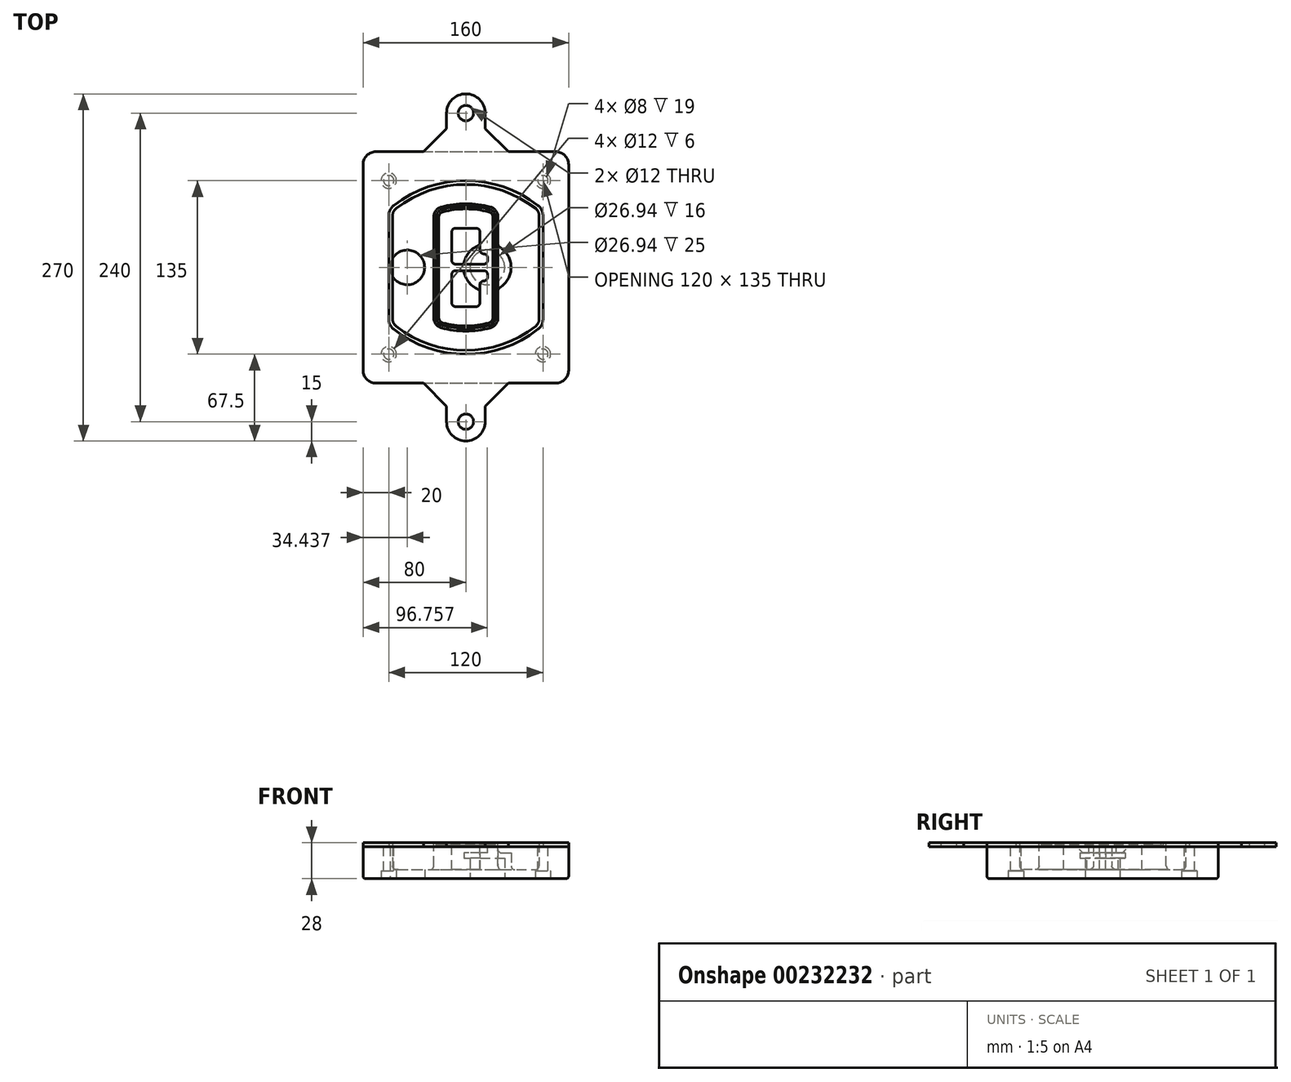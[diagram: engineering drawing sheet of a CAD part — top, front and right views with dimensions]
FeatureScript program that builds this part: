
annotation { "Feature Type Name" : "Feature", "Feature Type Description" : "" }
export const myFeature = defineFeature(function(context is Context, id is Id, definition is map)
    precondition{}
    {
        {
            var Q0;
            Q0=qCreatedBy(makeId("Top.planeOp"),FACE);
            var sketch = newSketch(context, id + "F0", { "sketchPlane" : qUnion([Q0])});
            skPoint(sketch, "E0.rect.middle", {"position": v(0, 0) * mm});
            skLineSegment(sketch, "E1.bottom", {"start": v(-70, -90) * mm, "end": v(70, -90) * mm});
            skLineSegment(sketch, "E1.top", {"start": v(-70, 90) * mm, "end": v(70, 90) * mm});
            skLineSegment(sketch, "E1.left", {"start": v(-80, -80) * mm, "end": v(-80, 80) * mm});
            skLineSegment(sketch, "E1.right", {"start": v(80, -80) * mm, "end": v(80, 80) * mm});
            skLineSegment(sketch, "E2", {"start": v(-80, 90) * mm, "end": v(80, -90) * mm, "construction": true});
            skLineSegment(sketch, "E3", {"start": v(80, 90) * mm, "end": v(-80, -90) * mm, "construction": true});
            skCircle(sketch, "E4", {"center": v(-60, 67.5) * mm, "radius": 4 * mm});
            skCircle(sketch, "E5", {"center": v(60, 67.5) * mm, "radius": 4 * mm});
            skCircle(sketch, "E6", {"center": v(60, -67.5) * mm, "radius": 4 * mm});
            skCircle(sketch, "E7", {"center": v(-60, -67.5) * mm, "radius": 4 * mm});
            skLineSegment(sketch, "E8", {"start": v(-60, 67.5) * mm, "end": v(60, 67.5) * mm, "construction": true});
            skLineSegment(sketch, "E9", {"start": v(60, 67.5) * mm, "end": v(60, -67.5) * mm, "construction": true});
            skLineSegment(sketch, "E10", {"start": v(60, -67.5) * mm, "end": v(-60, -67.5) * mm, "construction": true});
            skLineSegment(sketch, "E11", {"start": v(-60, -67.5) * mm, "end": v(-60, 67.5) * mm, "construction": true});
            skLineSegment(sketch, "E12", {"start": v(-60, 40.3) * mm, "end": v(-60, -40.3) * mm});
            skLineSegment(sketch, "E13", {"start": v(60, 40.3) * mm, "end": v(60, -40.3) * mm});
            skArc(sketch, "E14", {"start": v(56.15, 48.18) * mm, "mid": v(0, 67.5) * mm, "end": v(-56.15, 48.18) * mm});
            skArc(sketch, "E15", {"start": v(-56.15, -48.18) * mm, "mid": v(0, -67.5) * mm, "end": v(56.15, -48.18) * mm});
            skLineSegment(sketch, "E16", {"start": v(-60, 0) * mm, "end": v(60, 0) * mm, "construction": true});
            skPoint(sketch, "E17.visualSharp", {"position": v(-60, -45) * mm});
            skArc(sketch, "E17.filletArc", {"start": v(-60, -40.3) * mm, "mid": v(-58.99, -44.68) * mm, "end": v(-56.15, -48.18) * mm});
            skPoint(sketch, "E18.visualSharp", {"position": v(-60, 45) * mm});
            skArc(sketch, "E18.filletArc", {"start": v(-56.15, 48.18) * mm, "mid": v(-58.99, 44.68) * mm, "end": v(-60, 40.3) * mm});
            skPoint(sketch, "E19.visualSharp", {"position": v(60, 45) * mm});
            skArc(sketch, "E19.filletArc", {"start": v(60, 40.3) * mm, "mid": v(58.99, 44.68) * mm, "end": v(56.15, 48.18) * mm});
            skPoint(sketch, "E20.visualSharp", {"position": v(60, -45) * mm});
            skArc(sketch, "E20.filletArc", {"start": v(56.15, -48.18) * mm, "mid": v(58.99, -44.68) * mm, "end": v(60, -40.3) * mm});
            skPoint(sketch, "E21.visualSharp", {"position": v(-80, 90) * mm});
            skArc(sketch, "E21.filletArc", {"start": v(-70, 90) * mm, "mid": v(-77.07, 87.07) * mm, "end": v(-80, 80) * mm});
            skPoint(sketch, "E22.visualSharp", {"position": v(80, 90) * mm});
            skArc(sketch, "E22.filletArc", {"start": v(80, 80) * mm, "mid": v(77.07, 87.07) * mm, "end": v(70, 90) * mm});
            skPoint(sketch, "E23.visualSharp", {"position": v(80, -90) * mm});
            skArc(sketch, "E23.filletArc", {"start": v(70, -90) * mm, "mid": v(77.07, -87.07) * mm, "end": v(80, -80) * mm});
            skPoint(sketch, "E24.visualSharp", {"position": v(-80, -90) * mm});
            skArc(sketch, "E24.filletArc", {"start": v(-80, -80) * mm, "mid": v(-77.07, -87.07) * mm, "end": v(-70, -90) * mm});
            skArc(sketch, "E25.0", {"start": v(57, 40.3) * mm, "mid": v(56.3, 43.36) * mm, "end": v(54.3, 45.81) * mm});
            skLineSegment(sketch, "E25.1", {"start": v(57, 40.3) * mm, "end": v(57, -40.3) * mm});
            skArc(sketch, "E25.2", {"start": v(54.3, -45.81) * mm, "mid": v(56.3, -43.36) * mm, "end": v(57, -40.3) * mm});
            skArc(sketch, "E25.3", {"start": v(-54.3, -45.81) * mm, "mid": v(0, -64.5) * mm, "end": v(54.3, -45.81) * mm});
            skArc(sketch, "E25.4", {"start": v(-57, -40.3) * mm, "mid": v(-56.3, -43.36) * mm, "end": v(-54.3, -45.81) * mm});
            skArc(sketch, "E25.5", {"start": v(54.3, 45.81) * mm, "mid": v(0, 64.5) * mm, "end": v(-54.3, 45.81) * mm});
            skLineSegment(sketch, "E25.6", {"start": v(-57, 40.3) * mm, "end": v(-57, -40.3) * mm});
            skArc(sketch, "E25.7", {"start": v(-54.3, 45.81) * mm, "mid": v(-56.3, 43.36) * mm, "end": v(-57, 40.3) * mm});
            skArc(sketch, "E26.0", {"start": v(-58.62, 51.33) * mm, "mid": v(-62.58, 46.43) * mm, "end": v(-64, 40.3) * mm});
            skArc(sketch, "E26.1", {"start": v(58.62, 51.33) * mm, "mid": v(0, 71.5) * mm, "end": v(-58.62, 51.33) * mm});
            skArc(sketch, "E26.2", {"start": v(64, 40.3) * mm, "mid": v(62.58, 46.43) * mm, "end": v(58.62, 51.33) * mm});
            skLineSegment(sketch, "E26.3", {"start": v(64, 40.3) * mm, "end": v(64, -40.3) * mm});
            skArc(sketch, "E26.4", {"start": v(58.62, -51.33) * mm, "mid": v(62.58, -46.43) * mm, "end": v(64, -40.3) * mm});
            skLineSegment(sketch, "E26.5", {"start": v(-64, 40.3) * mm, "end": v(-64, -40.3) * mm});
            skArc(sketch, "E26.6", {"start": v(-58.62, -51.33) * mm, "mid": v(0, -71.5) * mm, "end": v(58.62, -51.33) * mm});
            skArc(sketch, "E26.7", {"start": v(-64, -40.3) * mm, "mid": v(-62.58, -46.43) * mm, "end": v(-58.62, -51.33) * mm});
            skSolve(sketch);
        }
        {
            var Q0;
            Q0=makeQuery(id+"F0.imprint","IMPRINT",FACE,{"disambiguationData":[TD([[makeQuery(id+"F0.imprint","IMPRINT",EDGE,{"derivedFrom":sQuery(id+"F0.wireOp",EDGE,"E1.bottom")}),1.0]])]});
            var Q1;
            Q1=makeQuery(id+"F0.imprint","IMPRINT",FACE,{"disambiguationData":[TD([[makeQuery(id+"F0.imprint","IMPRINT",EDGE,{"derivedFrom":sQuery(id+"F0.wireOp",EDGE,"E12")}),1.0]])]});
            var Q2;
            Q2=makeQuery(id+"F0.imprint","IMPRINT",FACE,{"disambiguationData":[TD([[makeQuery(id+"F0.imprint","IMPRINT",EDGE,{"derivedFrom":sQuery(id+"F0.wireOp",EDGE,"E25.0")}),1.0]])]});
            var Q3;
            Q3=makeQuery(id+"F0.imprint","IMPRINT",FACE,{"disambiguationData":[TD([[makeQuery(id+"F0.imprint","IMPRINT",EDGE,{"derivedFrom":sQuery(id+"F0.wireOp",EDGE,"E12")}),-1.0]])]});
            extrude(context, id + "F1", {"entities" : qUnion([Q0, Q1, Q2, Q3]), "oppositeDirection" : true, "depth" : 25 * mm});
        }
        {
            var Q0;
            Q0=makeQuery(id+"F0.imprint","IMPRINT",FACE,{"disambiguationData":[TD([[makeQuery(id+"F0.imprint","IMPRINT",EDGE,{"derivedFrom":sQuery(id+"F0.wireOp",EDGE,"E12")}),1.0]])]});
            extrude(context, id + "F2", {"entities" : qUnion([Q0]), "operationType" : NewBodyOperationType.ADD, "depth" : 3 * mm});
        }
        {
            var Q0;
            Q0=makeQuery(id+"F0.imprint","IMPRINT",FACE,{"disambiguationData":[TD([[makeQuery(id+"F0.imprint","IMPRINT",EDGE,{"derivedFrom":sQuery(id+"F0.wireOp",EDGE,"E25.0")}),1.0]])]});
            extrude(context, id + "F3", {"entities" : qUnion([Q0]), "operationType" : NewBodyOperationType.REMOVE, "oppositeDirection" : true, "depth" : 18 * mm});
        }
        {
            var Q0;
            Q0=makeQuery(id+"F2.opExtrude","CAP_FACE",FACE,{"disambiguationData":[OSD([sQuery(id+"F0.wireOp",EDGE,"E12"),sQuery(id+"F0.wireOp",EDGE,"E13"),sQuery(id+"F0.wireOp",EDGE,"E14"),sQuery(id+"F0.wireOp",EDGE,"E15"),sQuery(id+"F0.wireOp",EDGE,"E17.filletArc"),sQuery(id+"F0.wireOp",EDGE,"E18.filletArc"),sQuery(id+"F0.wireOp",EDGE,"E19.filletArc"),sQuery(id+"F0.wireOp",EDGE,"E20.filletArc"),sQuery(id+"F0.wireOp",EDGE,"E25.0"),sQuery(id+"F0.wireOp",EDGE,"E25.1"),sQuery(id+"F0.wireOp",EDGE,"E25.2"),sQuery(id+"F0.wireOp",EDGE,"E25.3"),sQuery(id+"F0.wireOp",EDGE,"E25.4"),sQuery(id+"F0.wireOp",EDGE,"E25.5"),sQuery(id+"F0.wireOp",EDGE,"E25.6"),sQuery(id+"F0.wireOp",EDGE,"E25.7")])],"isStart":false});
            var sketch = newSketch(context, id + "F4", { "sketchPlane" : qUnion([Q0])});
            skArc(sketch, "E27.0", {"start": v(-19.08, -46.97) * mm, "mid": v(0, -49.5) * mm, "end": v(19.08, -46.97) * mm});
            skArc(sketch, "E28.0", {"start": v(19.08, 46.97) * mm, "mid": v(0, 49.5) * mm, "end": v(-19.08, 46.97) * mm});
            skLineSegment(sketch, "E29", {"start": v(-25, 39.25) * mm, "end": v(-25, -39.25) * mm});
            skLineSegment(sketch, "E30", {"start": v(25, 39.25) * mm, "end": v(25, -39.25) * mm});
            skLineSegment(sketch, "E31", {"start": v(-25, 45.1) * mm, "end": v(25, 45.1) * mm, "construction": true});
            skLineSegment(sketch, "E32", {"start": v(-25, -45.1) * mm, "end": v(25, -45.1) * mm, "construction": true});
            skPoint(sketch, "E33.visualSharp", {"position": v(-25, 45.1) * mm});
            skArc(sketch, "E33.filletArc", {"start": v(-19.08, 46.97) * mm, "mid": v(-23.35, 44.11) * mm, "end": v(-25, 39.25) * mm});
            skPoint(sketch, "E34.visualSharp", {"position": v(25, 45.1) * mm});
            skArc(sketch, "E34.filletArc", {"start": v(25, 39.25) * mm, "mid": v(23.35, 44.11) * mm, "end": v(19.08, 46.97) * mm});
            skPoint(sketch, "E35.visualSharp", {"position": v(25, -45.1) * mm});
            skArc(sketch, "E35.filletArc", {"start": v(19.08, -46.97) * mm, "mid": v(23.35, -44.11) * mm, "end": v(25, -39.25) * mm});
            skPoint(sketch, "E36.visualSharp", {"position": v(-25, -45.1) * mm});
            skArc(sketch, "E36.filletArc", {"start": v(-25, -39.25) * mm, "mid": v(-23.35, -44.11) * mm, "end": v(-19.08, -46.97) * mm});
            skArc(sketch, "E37.0", {"start": v(54.3, 45.81) * mm, "mid": v(0, 64.5) * mm, "end": v(-54.3, 45.81) * mm});
            skArc(sketch, "E37.1", {"start": v(-54.3, 45.81) * mm, "mid": v(-56.3, 43.36) * mm, "end": v(-57, 40.3) * mm});
            skLineSegment(sketch, "E37.2", {"start": v(-57, 40.3) * mm, "end": v(-57, -40.3) * mm});
            skArc(sketch, "E37.3", {"start": v(-57, -40.3) * mm, "mid": v(-56.3, -43.36) * mm, "end": v(-54.3, -45.81) * mm});
            skArc(sketch, "E37.4", {"start": v(-54.3, -45.81) * mm, "mid": v(0, -64.5) * mm, "end": v(54.3, -45.81) * mm});
            skArc(sketch, "E37.5", {"start": v(54.3, -45.81) * mm, "mid": v(56.3, -43.36) * mm, "end": v(57, -40.3) * mm});
            skLineSegment(sketch, "E37.6", {"start": v(57, 40.3) * mm, "end": v(57, -40.3) * mm});
            skArc(sketch, "E37.7", {"start": v(57, 40.3) * mm, "mid": v(56.3, 43.36) * mm, "end": v(54.3, 45.81) * mm});
            skLineSegment(sketch, "E38.0", {"start": v(23, 39.25) * mm, "end": v(23, -39.25) * mm});
            skArc(sketch, "E38.1", {"start": v(18.56, -45.04) * mm, "mid": v(21.76, -42.9) * mm, "end": v(23, -39.25) * mm});
            skArc(sketch, "E38.2", {"start": v(-18.56, -45.04) * mm, "mid": v(0, -47.5) * mm, "end": v(18.56, -45.04) * mm});
            skArc(sketch, "E38.3", {"start": v(-23, -39.25) * mm, "mid": v(-21.76, -42.9) * mm, "end": v(-18.56, -45.04) * mm});
            skLineSegment(sketch, "E38.4", {"start": v(-23, 39.25) * mm, "end": v(-23, -39.25) * mm});
            skArc(sketch, "E38.5", {"start": v(23, 39.25) * mm, "mid": v(21.76, 42.9) * mm, "end": v(18.56, 45.04) * mm});
            skArc(sketch, "E38.6", {"start": v(-18.56, 45.04) * mm, "mid": v(-21.76, 42.9) * mm, "end": v(-23, 39.25) * mm});
            skArc(sketch, "E38.7", {"start": v(18.56, 45.04) * mm, "mid": v(0, 47.5) * mm, "end": v(-18.56, 45.04) * mm});
            skArc(sketch, "E39.0", {"start": v(21, 39.25) * mm, "mid": v(20.18, 41.68) * mm, "end": v(18.04, 43.1) * mm});
            skLineSegment(sketch, "E39.1", {"start": v(21, 39.25) * mm, "end": v(21, -39.25) * mm});
            skArc(sketch, "E39.2", {"start": v(18.04, -43.1) * mm, "mid": v(20.18, -41.68) * mm, "end": v(21, -39.25) * mm});
            skArc(sketch, "E39.3", {"start": v(-18.04, -43.1) * mm, "mid": v(0, -45.5) * mm, "end": v(18.04, -43.1) * mm});
            skArc(sketch, "E39.4", {"start": v(-21, -39.25) * mm, "mid": v(-20.18, -41.68) * mm, "end": v(-18.04, -43.1) * mm});
            skArc(sketch, "E39.5", {"start": v(18.04, 43.1) * mm, "mid": v(0, 45.5) * mm, "end": v(-18.04, 43.1) * mm});
            skLineSegment(sketch, "E39.6", {"start": v(-21, 39.25) * mm, "end": v(-21, -39.25) * mm});
            skArc(sketch, "E39.7", {"start": v(-18.04, 43.1) * mm, "mid": v(-20.18, 41.68) * mm, "end": v(-21, 39.25) * mm});
            skLineSegment(sketch, "E40", {"start": v(-25, 0) * mm, "end": v(25, 0) * mm, "construction": true});
            skLineSegment(sketch, "E41", {"start": v(-11, 5.5) * mm, "end": v(-11, 27.5) * mm});
            skLineSegment(sketch, "E42", {"start": v(-8, 30.5) * mm, "end": v(8, 30.5) * mm});
            skLineSegment(sketch, "E43", {"start": v(11, 27.5) * mm, "end": v(11, 13.5) * mm});
            skLineSegment(sketch, "E44", {"start": v(14, 10.5) * mm, "end": v(14, 10.5) * mm});
            skLineSegment(sketch, "E45", {"start": v(17, 7.5) * mm, "end": v(17, 5.5) * mm});
            skLineSegment(sketch, "E46", {"start": v(14, 2.5) * mm, "end": v(-8, 2.5) * mm});
            skPoint(sketch, "E47.visualSharp", {"position": v(-11, 30.5) * mm});
            skArc(sketch, "E47.filletArc", {"start": v(-8, 30.5) * mm, "mid": v(-10.12, 29.62) * mm, "end": v(-11, 27.5) * mm});
            skPoint(sketch, "E48.visualSharp", {"position": v(11, 30.5) * mm});
            skArc(sketch, "E48.filletArc", {"start": v(11, 27.5) * mm, "mid": v(10.12, 29.62) * mm, "end": v(8, 30.5) * mm});
            skPoint(sketch, "E49.visualSharp", {"position": v(11, 10.5) * mm});
            skArc(sketch, "E49.filletArc", {"start": v(11, 13.5) * mm, "mid": v(11.88, 11.38) * mm, "end": v(14, 10.5) * mm});
            skPoint(sketch, "E50.visualSharp", {"position": v(17, 10.5) * mm});
            skArc(sketch, "E50.filletArc", {"start": v(17, 7.5) * mm, "mid": v(16.12, 9.62) * mm, "end": v(14, 10.5) * mm});
            skPoint(sketch, "E51.visualSharp", {"position": v(17, 2.5) * mm});
            skArc(sketch, "E51.filletArc", {"start": v(14, 2.5) * mm, "mid": v(16.12, 3.38) * mm, "end": v(17, 5.5) * mm});
            skPoint(sketch, "E52.visualSharp", {"position": v(-11, 2.5) * mm});
            skArc(sketch, "E52.filletArc", {"start": v(-11, 5.5) * mm, "mid": v(-10.12, 3.38) * mm, "end": v(-8, 2.5) * mm});
            skLineSegment(sketch, "E53.0.MirrorCS", {"start": v(14, -2.5) * mm, "end": v(-8, -2.5) * mm});
            skArc(sketch, "E54.0.MirrorCS", {"start": v(-11, -5.5) * mm, "mid": v(-10.12, -3.38) * mm, "end": v(-8, -2.5) * mm});
            skLineSegment(sketch, "E55.0.MirrorCS", {"start": v(-11, -5.5) * mm, "end": v(-11, -27.5) * mm});
            skArc(sketch, "E56.0.MirrorCS", {"start": v(-8, -30.5) * mm, "mid": v(-10.12, -29.62) * mm, "end": v(-11, -27.5) * mm});
            skLineSegment(sketch, "E57.0.MirrorCS", {"start": v(-8, -30.5) * mm, "end": v(8, -30.5) * mm});
            skArc(sketch, "E58.0.MirrorCS", {"start": v(11, -27.5) * mm, "mid": v(10.12, -29.62) * mm, "end": v(8, -30.5) * mm});
            skLineSegment(sketch, "E59.0.MirrorCS", {"start": v(11, -27.5) * mm, "end": v(11, -13.5) * mm});
            skArc(sketch, "E60.0.MirrorCS", {"start": v(11, -13.5) * mm, "mid": v(11.88, -11.38) * mm, "end": v(14, -10.5) * mm});
            skArc(sketch, "E61.0.MirrorCS", {"start": v(17, -7.5) * mm, "mid": v(16.12, -9.62) * mm, "end": v(14, -10.5) * mm});
            skLineSegment(sketch, "E62.0.MirrorCS", {"start": v(17, -7.5) * mm, "end": v(17, -5.5) * mm});
            skArc(sketch, "E63.0.MirrorCS", {"start": v(14, -2.5) * mm, "mid": v(16.12, -3.38) * mm, "end": v(17, -5.5) * mm});
            skSolve(sketch);
        }
        {
            var Q0;
            Q0=makeQuery(id+"F4.imprint","IMPRINT",FACE,{"disambiguationData":[TD([[makeQuery(id+"F4.imprint","IMPRINT",EDGE,{"derivedFrom":sQuery(id+"F4.wireOp",EDGE,"E27.0")}),1.0]])]});
            var Q1;
            Q1=makeQuery(id+"F4.imprint","IMPRINT",FACE,{"disambiguationData":[TD([[makeQuery(id+"F4.imprint","IMPRINT",EDGE,{"derivedFrom":sQuery(id+"F4.wireOp",EDGE,"E38.0")}),-1.0]])]});
            var Q2;
            Q2=makeQuery(id+"F4.imprint","IMPRINT",FACE,{"disambiguationData":[TD([[makeQuery(id+"F4.imprint","IMPRINT",EDGE,{"derivedFrom":sQuery(id+"F4.wireOp",EDGE,"E39.0")}),1.0]])]});
            extrude(context, id + "F5", {"entities" : qUnion([Q0, Q1, Q2]), "operationType" : NewBodyOperationType.ADD, "endBound" : BoundingType.UP_TO_NEXT, "oppositeDirection" : true, "depth" : 25 * mm});
        }
        {
            var Q0;
            Q0=makeQuery(id+"F4.imprint","IMPRINT",FACE,{"disambiguationData":[TD([[makeQuery(id+"F4.imprint","IMPRINT",EDGE,{"derivedFrom":sQuery(id+"F4.wireOp",EDGE,"E38.0")}),-1.0]])]});
            extrude(context, id + "F6", {"entities" : qUnion([Q0]), "operationType" : NewBodyOperationType.REMOVE, "oppositeDirection" : true, "depth" : 2 * mm});
        }
        {
            var Q0;
            Q0=makeQuery(id+"F1.opExtrude","CAP_FACE",FACE,{"disambiguationData":[OSD([sQuery(id+"F0.wireOp",EDGE,"E1.bottom"),sQuery(id+"F0.wireOp",EDGE,"E1.top"),sQuery(id+"F0.wireOp",EDGE,"E1.left"),sQuery(id+"F0.wireOp",EDGE,"E1.right"),sQuery(id+"F0.wireOp",EDGE,"E4"),sQuery(id+"F0.wireOp",EDGE,"E5"),sQuery(id+"F0.wireOp",EDGE,"E6"),sQuery(id+"F0.wireOp",EDGE,"E7"),sQuery(id+"F0.wireOp",EDGE,"E21.filletArc"),sQuery(id+"F0.wireOp",EDGE,"E22.filletArc"),sQuery(id+"F0.wireOp",EDGE,"E23.filletArc"),sQuery(id+"F0.wireOp",EDGE,"E24.filletArc")])],"isStart":false});
            var sketch = newSketch(context, id + "F7", { "sketchPlane" : qUnion([Q0])});
            skCircle(sketch, "E64", {"center": v(16.76, 0) * mm, "radius": 13.47 * mm});
            skCircle(sketch, "E65", {"center": v(-45.56, 0) * mm, "radius": 13.47 * mm});
            skLineSegment(sketch, "E66", {"start": v(80, 0) * mm, "end": v(-80, 0) * mm});
            skCircle(sketch, "E67", {"center": v(16.76, 0) * mm, "radius": 18.47 * mm});
            skCircle(sketch, "E68", {"center": v(60, -67.5) * mm, "radius": 6 * mm});
            skCircle(sketch, "E69", {"center": v(-60, -67.5) * mm, "radius": 6 * mm});
            skCircle(sketch, "E70", {"center": v(-60, 67.5) * mm, "radius": 6 * mm});
            skCircle(sketch, "E71", {"center": v(60, 67.5) * mm, "radius": 6 * mm});
            skSolve(sketch);
        }
        {
            var Q0;
            {var subQ1=sQuery(id+"F7.wireOp",EDGE,"E66");var subQ4=sQuery(id+"F7.wireOp",EDGE,"E64");var subQ6=makeQuery(id+"F7.imprint","INTERSECT",VERTEX,{"disambiguationData":[OD(0.0)],"derivedFrom":[subQ4,subQ1]});Q0=makeQuery(id+"F7.imprint","IMPRINT",FACE,{"disambiguationData":[TD([[makeQuery(id+"F7.imprint","IMPRINT",EDGE,{"disambiguationData":[TD([[subQ6,-1.0]])],"derivedFrom":subQ4}),-1.0]])]});}
            var Q1;
            {var subQ0=sQuery(id+"F7.wireOp",EDGE,"E66");var subQ1=sQuery(id+"F7.wireOp",EDGE,"E64");var subQ3=makeQuery(id+"F7.imprint","INTERSECT",VERTEX,{"disambiguationData":[OD(0.0)],"derivedFrom":[subQ1,subQ0]});Q1=makeQuery(id+"F7.imprint","IMPRINT",FACE,{"disambiguationData":[TD([[makeQuery(id+"F7.imprint","IMPRINT",EDGE,{"disambiguationData":[TD([[subQ3,-1.0]])],"derivedFrom":subQ1}),1.0]])]});}
            var Q2;
            {var subQ0=sQuery(id+"F7.wireOp",EDGE,"E66");var subQ1=sQuery(id+"F7.wireOp",EDGE,"E64");var subQ3=makeQuery(id+"F7.imprint","INTERSECT",VERTEX,{"disambiguationData":[OD(0.0)],"derivedFrom":[subQ1,subQ0]});Q2=makeQuery(id+"F7.imprint","IMPRINT",FACE,{"disambiguationData":[TD([[makeQuery(id+"F7.imprint","IMPRINT",EDGE,{"disambiguationData":[TD([[subQ3,1.0]])],"derivedFrom":subQ1}),1.0]])]});}
            var Q3;
            {var subQ1=sQuery(id+"F7.wireOp",EDGE,"E66");var subQ4=sQuery(id+"F7.wireOp",EDGE,"E64");var subQ6=makeQuery(id+"F7.imprint","INTERSECT",VERTEX,{"disambiguationData":[OD(0.0)],"derivedFrom":[subQ4,subQ1]});Q3=makeQuery(id+"F7.imprint","IMPRINT",FACE,{"disambiguationData":[TD([[makeQuery(id+"F7.imprint","IMPRINT",EDGE,{"disambiguationData":[TD([[subQ6,1.0]])],"derivedFrom":subQ4}),-1.0]])]});}
            extrude(context, id + "F8", {"entities" : qUnion([Q0, Q1, Q2, Q3]), "operationType" : NewBodyOperationType.ADD, "oppositeDirection" : true, "depth" : 20 * mm});
        }
        {
            var Q0;
            {var subQ0=sQuery(id+"F7.wireOp",EDGE,"E66");var subQ1=sQuery(id+"F7.wireOp",EDGE,"E64");var subQ3=makeQuery(id+"F7.imprint","INTERSECT",VERTEX,{"disambiguationData":[OD(0.0)],"derivedFrom":[subQ1,subQ0]});Q0=makeQuery(id+"F7.imprint","IMPRINT",FACE,{"disambiguationData":[TD([[makeQuery(id+"F7.imprint","IMPRINT",EDGE,{"disambiguationData":[TD([[subQ3,-1.0]])],"derivedFrom":subQ1}),1.0]])]});}
            var Q1;
            {var subQ0=sQuery(id+"F7.wireOp",EDGE,"E66");var subQ1=sQuery(id+"F7.wireOp",EDGE,"E64");var subQ3=makeQuery(id+"F7.imprint","INTERSECT",VERTEX,{"disambiguationData":[OD(0.0)],"derivedFrom":[subQ1,subQ0]});Q1=makeQuery(id+"F7.imprint","IMPRINT",FACE,{"disambiguationData":[TD([[makeQuery(id+"F7.imprint","IMPRINT",EDGE,{"disambiguationData":[TD([[subQ3,1.0]])],"derivedFrom":subQ1}),1.0]])]});}
            extrude(context, id + "F9", {"entities" : qUnion([Q0, Q1]), "operationType" : NewBodyOperationType.REMOVE, "oppositeDirection" : true, "depth" : 16 * mm});
        }
        {
            var Q0;
            {var subQ0=sQuery(id+"F7.wireOp",EDGE,"E66");var subQ1=sQuery(id+"F7.wireOp",EDGE,"E65");var subQ3=makeQuery(id+"F7.imprint","INTERSECT",VERTEX,{"disambiguationData":[OD(0.0)],"derivedFrom":[subQ1,subQ0]});Q0=makeQuery(id+"F7.imprint","IMPRINT",FACE,{"disambiguationData":[TD([[makeQuery(id+"F7.imprint","IMPRINT",EDGE,{"disambiguationData":[TD([[subQ3,-1.0]])],"derivedFrom":subQ1}),1.0]])]});}
            var Q1;
            {var subQ0=sQuery(id+"F7.wireOp",EDGE,"E66");var subQ1=sQuery(id+"F7.wireOp",EDGE,"E65");var subQ3=makeQuery(id+"F7.imprint","INTERSECT",VERTEX,{"disambiguationData":[OD(0.0)],"derivedFrom":[subQ1,subQ0]});Q1=makeQuery(id+"F7.imprint","IMPRINT",FACE,{"disambiguationData":[TD([[makeQuery(id+"F7.imprint","IMPRINT",EDGE,{"disambiguationData":[TD([[subQ3,1.0]])],"derivedFrom":subQ1}),1.0]])]});}
            extrude(context, id + "F10", {"entities" : qUnion([Q0, Q1]), "operationType" : NewBodyOperationType.REMOVE, "oppositeDirection" : true, "depth" : 25 * mm});
        }
        {
            var Q0;
            Q0=makeQuery(id+"F7.imprint","IMPRINT",FACE,{"disambiguationData":[TD([[makeQuery(id+"F7.imprint","IMPRINT",EDGE,{"derivedFrom":sQuery(id+"F7.wireOp",EDGE,"E68")}),1.0]])]});
            var Q1;
            Q1=makeQuery(id+"F7.imprint","IMPRINT",FACE,{"disambiguationData":[TD([[makeQuery(id+"F7.imprint","IMPRINT",EDGE,{"derivedFrom":makeQuery(id+"F1.opExtrude","CAP_EDGE",EDGE,{"disambiguationData":[OSD([sQuery(id+"F0.wireOp",EDGE,"E5")])],"isStart":false})}),-1.0]])]});
            var Q2;
            Q2=makeQuery(id+"F7.imprint","IMPRINT",FACE,{"disambiguationData":[TD([[makeQuery(id+"F7.imprint","IMPRINT",EDGE,{"derivedFrom":sQuery(id+"F7.wireOp",EDGE,"E69")}),1.0]])]});
            var Q3;
            Q3=makeQuery(id+"F7.imprint","IMPRINT",FACE,{"disambiguationData":[TD([[makeQuery(id+"F7.imprint","IMPRINT",EDGE,{"derivedFrom":makeQuery(id+"F1.opExtrude","CAP_EDGE",EDGE,{"disambiguationData":[OSD([sQuery(id+"F0.wireOp",EDGE,"E4")])],"isStart":false})}),-1.0]])]});
            var Q4;
            Q4=makeQuery(id+"F7.imprint","IMPRINT",FACE,{"disambiguationData":[TD([[makeQuery(id+"F7.imprint","IMPRINT",EDGE,{"derivedFrom":sQuery(id+"F7.wireOp",EDGE,"E70")}),1.0]])]});
            var Q5;
            Q5=makeQuery(id+"F7.imprint","IMPRINT",FACE,{"disambiguationData":[TD([[makeQuery(id+"F7.imprint","IMPRINT",EDGE,{"derivedFrom":makeQuery(id+"F1.opExtrude","CAP_EDGE",EDGE,{"disambiguationData":[OSD([sQuery(id+"F0.wireOp",EDGE,"E7")])],"isStart":false})}),-1.0]])]});
            var Q6;
            Q6=makeQuery(id+"F7.imprint","IMPRINT",FACE,{"disambiguationData":[TD([[makeQuery(id+"F7.imprint","IMPRINT",EDGE,{"derivedFrom":sQuery(id+"F7.wireOp",EDGE,"E71")}),1.0]])]});
            var Q7;
            Q7=makeQuery(id+"F7.imprint","IMPRINT",FACE,{"disambiguationData":[TD([[makeQuery(id+"F7.imprint","IMPRINT",EDGE,{"derivedFrom":makeQuery(id+"F1.opExtrude","CAP_EDGE",EDGE,{"disambiguationData":[OSD([sQuery(id+"F0.wireOp",EDGE,"E6")])],"isStart":false})}),-1.0]])]});
            extrude(context, id + "F11", {"entities" : qUnion([Q0, Q1, Q2, Q3, Q4, Q5, Q6, Q7]), "operationType" : NewBodyOperationType.REMOVE, "oppositeDirection" : true, "depth" : 6 * mm});
        }
        {
            var Q0;
            Q0=makeQuery(id+"F9.boolean.opBoolean","COPY",FACE,{"derivedFrom":makeQuery(id+"F9.opExtrude","CAP_FACE",FACE,{"disambiguationData":[OSD([sQuery(id+"F7.wireOp",EDGE,"E64")])],"isStart":false})});
            var sketch = newSketch(context, id + "F12", { "sketchPlane" : qUnion([Q0])});
            skArc(sketch, "E72.0", {"start": v(11, 17.55) * mm, "mid": v(2.57, 11.82) * mm, "end": v(-1.54, 2.5) * mm});
            skArc(sketch, "E72.1", {"start": v(-1.54, -2.5) * mm, "mid": v(2.57, -11.82) * mm, "end": v(11, -17.55) * mm});
            skLineSegment(sketch, "E73", {"start": v(-1.54, -2.5) * mm, "end": v(14, -2.5) * mm});
            skLineSegment(sketch, "E74.0", {"start": v(14, 2.5) * mm, "end": v(-1.54, 2.5) * mm});
            skArc(sketch, "E74.1", {"start": v(14, 2.5) * mm, "mid": v(16.12, 3.38) * mm, "end": v(17, 5.5) * mm});
            skLineSegment(sketch, "E74.2", {"start": v(17, 7.5) * mm, "end": v(17, 5.5) * mm});
            skArc(sketch, "E74.3", {"start": v(17, 7.5) * mm, "mid": v(16.12, 9.62) * mm, "end": v(14, 10.5) * mm});
            skArc(sketch, "E74.4", {"start": v(11, 13.5) * mm, "mid": v(11.88, 11.38) * mm, "end": v(14, 10.5) * mm});
            skLineSegment(sketch, "E74.5", {"start": v(11, 17.55) * mm, "end": v(11, 13.5) * mm});
            skLineSegment(sketch, "E74.7", {"start": v(14, -2.5) * mm, "end": v(-1.54, -2.5) * mm});
            skArc(sketch, "E74.8", {"start": v(14, -2.5) * mm, "mid": v(16.12, -3.38) * mm, "end": v(17, -5.5) * mm});
            skLineSegment(sketch, "E74.9", {"start": v(17, -7.5) * mm, "end": v(17, -5.5) * mm});
            skArc(sketch, "E74.10", {"start": v(17, -7.5) * mm, "mid": v(16.12, -9.62) * mm, "end": v(14, -10.5) * mm});
            skArc(sketch, "E74.11", {"start": v(11, -13.5) * mm, "mid": v(11.88, -11.38) * mm, "end": v(14, -10.5) * mm});
            skLineSegment(sketch, "E74.12", {"start": v(11, -17.55) * mm, "end": v(11, -13.5) * mm});
            skPoint(sketch, "E75.orphan", {"position": v(11, -27.5) * mm});
            skPoint(sketch, "E76.orphan", {"position": v(-8, -2.5) * mm});
            skPoint(sketch, "E77.orphan", {"position": v(-8, 2.5) * mm});
            skPoint(sketch, "E78.orphan", {"position": v(11, 27.5) * mm});
            skSolve(sketch);
        }
        {
            var Q0;
            {var subQ7=sQuery(id+"F12.wireOp",EDGE,"E72.0");var subQ14=sQuery(id+"F12.wireOp",EDGE,"E72.1");var subQ16=sQuery(id+"F12.wireOp",EDGE,"E74.1");var subQ18=sQuery(id+"F12.wireOp",EDGE,"E74.8");Q0=qUnion([makeQuery(id+"F12.imprint","IMPRINT",FACE,{"disambiguationData":[TD([[makeQuery(id+"F12.imprint","IMPRINT",EDGE,{"derivedFrom":subQ7}),1.0]])]}),makeQuery(id+"F12.imprint","IMPRINT",FACE,{"disambiguationData":[TD([[makeQuery(id+"F12.imprint","IMPRINT",EDGE,{"derivedFrom":subQ14}),1.0]])]}),makeQuery(id+"F12.imprint","IMPRINT",FACE,{"disambiguationData":[TD([[makeQuery(id+"F12.imprint","IMPRINT",EDGE,{"derivedFrom":subQ16}),1.0]])]}),makeQuery(id+"F12.imprint","IMPRINT",FACE,{"disambiguationData":[TD([[makeQuery(id+"F12.imprint","IMPRINT",EDGE,{"derivedFrom":subQ18}),-1.0]])]})]);}
            var Q1;
            Q1=makeQuery(id+"F5.boolean.opBoolean","SPLIT",FACE,{"disambiguationData":[TD([makeQuery(id+"F5.opExtrude","SWEPT_FACE",FACE,{"disambiguationData":[OSD([sQuery(id+"F4.wireOp",EDGE,"E41")])]})])],"derivedFrom":makeQuery(id+"F3.boolean.opBoolean","COPY",FACE,{"derivedFrom":makeQuery(id+"F3.opExtrude","CAP_FACE",FACE,{"disambiguationData":[OSD([sQuery(id+"F0.wireOp",EDGE,"E25.0"),sQuery(id+"F0.wireOp",EDGE,"E25.1"),sQuery(id+"F0.wireOp",EDGE,"E25.2"),sQuery(id+"F0.wireOp",EDGE,"E25.3"),sQuery(id+"F0.wireOp",EDGE,"E25.4"),sQuery(id+"F0.wireOp",EDGE,"E25.5"),sQuery(id+"F0.wireOp",EDGE,"E25.6"),sQuery(id+"F0.wireOp",EDGE,"E25.7")])],"isStart":false})})});
            extrude(context, id + "F13", {"entities" : qUnion([Q0]), "operationType" : NewBodyOperationType.REMOVE, "endBound" : BoundingType.UP_TO_SURFACE, "endBoundEntityFace" : qUnion([Q1]), "depth" : 25 * mm});
        }
        {
            var Q0;
            Q0=makeQuery(id+"F3.boolean.opBoolean","COPY",EDGE,{"derivedFrom":makeQuery(id+"F3.opExtrude","CAP_EDGE",EDGE,{"disambiguationData":[OSD([sQuery(id+"F0.wireOp",EDGE,"E25.6")])],"isStart":false})});
            var Q1;
            Q1=makeQuery(id+"F8.boolean.opBoolean","INTERSECT",EDGE,{"derivedFrom":[makeQuery(id+"F5.opExtrude","SWEPT_FACE",FACE,{"disambiguationData":[OSD([sQuery(id+"F4.wireOp",EDGE,"E30")])]}),makeQuery(id+"F8.opExtrude","CAP_FACE",FACE,{"disambiguationData":[OSD([sQuery(id+"F7.wireOp",EDGE,"E67")])],"isStart":false})]});
            var Q2;
            Q2=makeQuery(id+"F8.boolean.opBoolean","INTERSECT",EDGE,{"disambiguationData":[OD(1.0)],"derivedFrom":[makeQuery(id+"F5.opExtrude","SWEPT_FACE",FACE,{"disambiguationData":[OSD([sQuery(id+"F4.wireOp",EDGE,"E30")])]}),makeQuery(id+"F8.opExtrude","SWEPT_FACE",FACE,{"disambiguationData":[OSD([sQuery(id+"F7.wireOp",EDGE,"E67")])]})]});
            var Q3;
            {var subQ0=sQuery(id+"F4.wireOp",EDGE,"E30");Q3=makeQuery(id+"F8.boolean.opBoolean","SPLIT",EDGE,{"disambiguationData":[TD([makeQuery(id+"F5.opExtrude","SWEPT_FACE",FACE,{"disambiguationData":[OSD([sQuery(id+"F4.wireOp",EDGE,"E35.filletArc")])]})])],"derivedFrom":makeQuery(id+"F5.opExtrude","CAP_EDGE",EDGE,{"disambiguationData":[OSD([subQ0])],"isStart":false})});}
            var Q4;
            {var subQ0=sQuery(id+"F0.wireOp",EDGE,"E25.7");var subQ1=sQuery(id+"F0.wireOp",EDGE,"E25.1");var subQ2=sQuery(id+"F0.wireOp",EDGE,"E25.6");var subQ3=sQuery(id+"F0.wireOp",EDGE,"E25.5");var subQ4=sQuery(id+"F0.wireOp",EDGE,"E25.4");var subQ5=sQuery(id+"F0.wireOp",EDGE,"E25.0");var subQ6=sQuery(id+"F0.wireOp",EDGE,"E25.2");var subQ7=sQuery(id+"F0.wireOp",EDGE,"E25.3");Q4=makeQuery(id+"F8.boolean.opBoolean","INTERSECT",EDGE,{"derivedFrom":[makeQuery(id+"F5.boolean.opBoolean","SPLIT",FACE,{"disambiguationData":[TD([makeQuery(id+"F2.opExtrude","SWEPT_FACE",FACE,{"disambiguationData":[OSD([subQ5])]})])],"derivedFrom":makeQuery(id+"F3.boolean.opBoolean","COPY",FACE,{"derivedFrom":makeQuery(id+"F3.opExtrude","CAP_FACE",FACE,{"disambiguationData":[OSD([subQ5,subQ1,subQ6,subQ7,subQ4,subQ3,subQ2,subQ0])],"isStart":false})})}),makeQuery(id+"F8.opExtrude","SWEPT_FACE",FACE,{"disambiguationData":[OSD([sQuery(id+"F7.wireOp",EDGE,"E67")])]})]});}
            var Q5;
            Q5=makeQuery(id+"F8.boolean.opBoolean","INTERSECT",EDGE,{"disambiguationData":[OD(0.0)],"derivedFrom":[makeQuery(id+"F5.opExtrude","SWEPT_FACE",FACE,{"disambiguationData":[OSD([sQuery(id+"F4.wireOp",EDGE,"E30")])]}),makeQuery(id+"F8.opExtrude","SWEPT_FACE",FACE,{"disambiguationData":[OSD([sQuery(id+"F7.wireOp",EDGE,"E67")])]})]});
            fillet(context, id + "F14", {"entities" : qUnion([Q0, Q1, Q2, Q3, Q4, Q5]), "radius" : 3 * mm, "tangentPropagation" : true, "allowEdgeOverflow" : false});
        }
        {
            var Q0;
            Q0=makeQuery(id+"F1.opExtrude","CAP_EDGE",EDGE,{"disambiguationData":[OSD([sQuery(id+"F0.wireOp",EDGE,"E1.bottom")])],"isStart":false});
            fillet(context, id + "F15", {"entities" : qUnion([Q0]), "radius" : 2 * mm, "tangentPropagation" : true, "allowEdgeOverflow" : false});
        }
        {
            var Q0;
            {var subQ0=sQuery(id+"F0.wireOp",EDGE,"E22.filletArc");var subQ1=sQuery(id+"F0.wireOp",EDGE,"E7");var subQ2=sQuery(id+"F0.wireOp",EDGE,"E6");var subQ3=sQuery(id+"F0.wireOp",EDGE,"E5");var subQ4=sQuery(id+"F0.wireOp",EDGE,"E4");var subQ5=sQuery(id+"F0.wireOp",EDGE,"E1.bottom");var subQ6=sQuery(id+"F0.wireOp",EDGE,"E21.filletArc");var subQ7=sQuery(id+"F0.wireOp",EDGE,"E1.top");var subQ8=sQuery(id+"F0.wireOp",EDGE,"E1.left");var subQ9=sQuery(id+"F0.wireOp",EDGE,"E1.right");var subQ10=sQuery(id+"F0.wireOp",EDGE,"E23.filletArc");var subQ11=sQuery(id+"F0.wireOp",EDGE,"E24.filletArc");Q0=makeQuery(id+"F2.boolean.opBoolean","SPLIT",FACE,{"disambiguationData":[TD([makeQuery(id+"F1.opExtrude","SWEPT_FACE",FACE,{"disambiguationData":[OSD([subQ5])]})])],"derivedFrom":makeQuery(id+"F1.opExtrude","CAP_FACE",FACE,{"disambiguationData":[OSD([subQ5,subQ7,subQ8,subQ9,subQ4,subQ3,subQ2,subQ1,subQ6,subQ0,subQ10,subQ11])],"isStart":true})});}
            var sketch = newSketch(context, id + "F16", { "sketchPlane" : qUnion([Q0])});
            skLineSegment(sketch, "E79.0", {"start": v(-70, 90) * mm, "end": v(70, 90) * mm});
            skArc(sketch, "E79.1", {"start": v(-70, 90) * mm, "mid": v(-77.07, 87.07) * mm, "end": v(-80, 80) * mm});
            skLineSegment(sketch, "E79.2", {"start": v(-80, -80) * mm, "end": v(-80, 80) * mm});
            skArc(sketch, "E79.3", {"start": v(80, 80) * mm, "mid": v(77.07, 87.07) * mm, "end": v(70, 90) * mm});
            skLineSegment(sketch, "E79.4", {"start": v(80, -80) * mm, "end": v(80, 80) * mm});
            skArc(sketch, "E79.5", {"start": v(-80, -80) * mm, "mid": v(-77.07, -87.07) * mm, "end": v(-70, -90) * mm});
            skLineSegment(sketch, "E79.6", {"start": v(-70, -90) * mm, "end": v(70, -90) * mm});
            skArc(sketch, "E79.7", {"start": v(70, -90) * mm, "mid": v(77.07, -87.07) * mm, "end": v(80, -80) * mm});
            skArc(sketch, "E79.8", {"start": v(56.15, 48.18) * mm, "mid": v(0, 67.5) * mm, "end": v(-56.15, 48.18) * mm});
            skArc(sketch, "E79.9", {"start": v(-56.15, 48.18) * mm, "mid": v(-58.99, 44.68) * mm, "end": v(-60, 40.3) * mm});
            skLineSegment(sketch, "E79.10", {"start": v(-60, 40.3) * mm, "end": v(-60, -40.3) * mm});
            skLineSegment(sketch, "E79.11", {"start": v(60, 40.3) * mm, "end": v(60, -40.3) * mm});
            skArc(sketch, "E79.12", {"start": v(60, 40.3) * mm, "mid": v(58.99, 44.68) * mm, "end": v(56.15, 48.18) * mm});
            skArc(sketch, "E79.13", {"start": v(-56.15, -48.18) * mm, "mid": v(0, -67.5) * mm, "end": v(56.15, -48.18) * mm});
            skArc(sketch, "E79.14", {"start": v(56.15, -48.18) * mm, "mid": v(58.99, -44.68) * mm, "end": v(60, -40.3) * mm});
            skArc(sketch, "E79.15", {"start": v(-60, -40.3) * mm, "mid": v(-58.99, -44.68) * mm, "end": v(-56.15, -48.18) * mm});
            skLineSegment(sketch, "E80", {"start": v(0, 90) * mm, "end": v(0, 120) * mm});
            skCircle(sketch, "E81", {"center": v(0, 120) * mm, "radius": 6 * mm});
            skLineSegment(sketch, "E82", {"start": v(-33, 90) * mm, "end": v(-15, 108) * mm});
            skLineSegment(sketch, "E83", {"start": v(33, 90) * mm, "end": v(15, 108) * mm});
            skLineSegment(sketch, "E84", {"start": v(-15, 108) * mm, "end": v(-15, 120) * mm});
            skLineSegment(sketch, "E85", {"start": v(15, 108) * mm, "end": v(15, 120) * mm});
            skArc(sketch, "E86", {"start": v(15, 120) * mm, "mid": v(0, 135) * mm, "end": v(-15, 120) * mm});
            skLineSegment(sketch, "E87", {"start": v(0, 0) * mm, "end": v(-80, 0) * mm});
            skLineSegment(sketch, "E88", {"start": v(0, 0) * mm, "end": v(80, 0) * mm});
            skLineSegment(sketch, "E89.MirrorCS", {"start": v(0, -90) * mm, "end": v(0, -120) * mm});
            skLineSegment(sketch, "E90.MirrorCS", {"start": v(-33, -90) * mm, "end": v(-15, -108) * mm});
            skLineSegment(sketch, "E91.MirrorCS", {"start": v(-15, -108) * mm, "end": v(-15, -120) * mm});
            skLineSegment(sketch, "E92.MirrorCS", {"start": v(15, -108) * mm, "end": v(15, -120) * mm});
            skLineSegment(sketch, "E93.MirrorCS", {"start": v(33, -90) * mm, "end": v(15, -108) * mm});
            skArc(sketch, "E94.MirrorCS", {"start": v(15, -120) * mm, "mid": v(0, -135) * mm, "end": v(-15, -120) * mm});
            skCircle(sketch, "E95.MirrorC", {"center": v(0, -120) * mm, "radius": 6 * mm});
            skSolve(sketch);
        }
        {
            var Q0;
            Q0 = qSketchRegion(id + "F16", true);
            var Q1;
            Q1=makeQuery(id+"F2.opExtrude","CAP_FACE",FACE,{"disambiguationData":[OSD([sQuery(id+"F0.wireOp",EDGE,"E12"),sQuery(id+"F0.wireOp",EDGE,"E13"),sQuery(id+"F0.wireOp",EDGE,"E14"),sQuery(id+"F0.wireOp",EDGE,"E15"),sQuery(id+"F0.wireOp",EDGE,"E17.filletArc"),sQuery(id+"F0.wireOp",EDGE,"E18.filletArc"),sQuery(id+"F0.wireOp",EDGE,"E19.filletArc"),sQuery(id+"F0.wireOp",EDGE,"E20.filletArc"),sQuery(id+"F0.wireOp",EDGE,"E25.0"),sQuery(id+"F0.wireOp",EDGE,"E25.1"),sQuery(id+"F0.wireOp",EDGE,"E25.2"),sQuery(id+"F0.wireOp",EDGE,"E25.3"),sQuery(id+"F0.wireOp",EDGE,"E25.4"),sQuery(id+"F0.wireOp",EDGE,"E25.5"),sQuery(id+"F0.wireOp",EDGE,"E25.6"),sQuery(id+"F0.wireOp",EDGE,"E25.7")])],"isStart":false});
            extrude(context, id + "F17", {"entities" : qUnion([Q0]), "endBound" : BoundingType.UP_TO_SURFACE, "endBoundEntityFace" : qUnion([Q1]), "depth" : 25 * mm});
        }
    });
